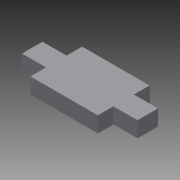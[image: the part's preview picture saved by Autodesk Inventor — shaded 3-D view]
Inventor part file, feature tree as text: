
AUTODESK INVENTOR PART (.ipt)
format: ipt  version: 2013 (Build 170138000, 138)  size: 99,328 bytes
history: native  units: mm
features: other x2, extrude x1, sketch x1
ambient origin geometry x8: Origin, YZ Plane, XZ Plane, XY Plane, X Axis, Y Axis, Z Axis, Center Point
feature tree (4):
  other  "Blocks"
  extrude  "Extrusion6"  Depth=3.0mm
  sketch  "Sketch1"  dims[d3=3.0mm d5=3.0mm d22=22.5mm d23=12.4mm d24=4.5mm d25=4.5mm d26=2.0mm d27=2.0mm d42=24.0mm d43=4.25mm d44=14.0mm d45=3.25mm d46=3.25mm d47=0.0mm]
  other  "Block1"
